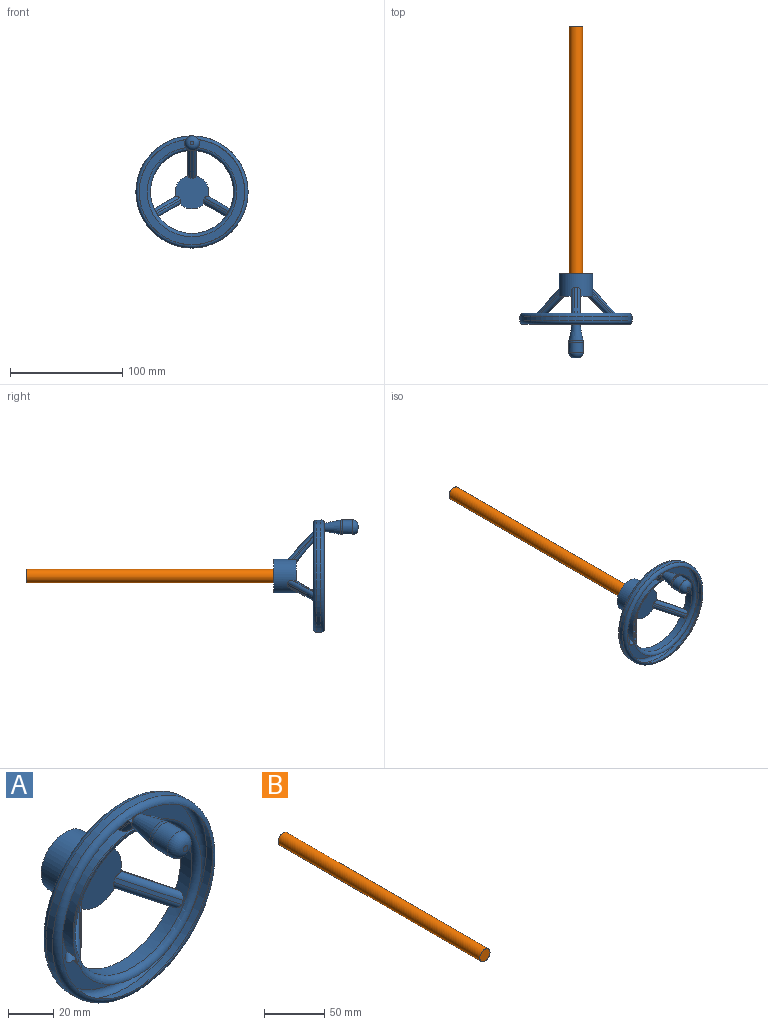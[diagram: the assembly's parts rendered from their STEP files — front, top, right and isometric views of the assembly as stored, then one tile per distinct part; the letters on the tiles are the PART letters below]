
ASSEMBLY  parts=2 mates=1
PART A: 47 faces, bbox 108.3x75x108.3 mm
  f0: cylinder r=15mm len=30mm, axis (0,1,0), area 1712.4mm2, adj f1,f4,f5,f6,f7,f14,f15,f16
  f1: plane 30x29.57mm, normal (0,-1,0), area 663.3mm2, adj f0,f12,f17,f22,f28,f30,f32,f34
  f2: plane 12x12mm, normal (0,1,0), area 113.1mm2, adj f3
  f3: cylinder r=6mm len=15mm, axis (0,1,0), area 565.5mm2, adj f2,f4
  f4: plane 30x30mm, normal (0,1,0), area 593.8mm2, adj f0,f3
  f5: plane 3.25x1.05mm, normal (0,0.32,-0.95), area 0.4mm2, adj f0,f13,f38
  f6: plane 2.99x1.32mm, normal (0.82,0.32,0.47), area 0.4mm2, adj f0,f18,f31
  f7: plane 2.63x1.93mm, normal (-0.82,0.32,0.47), area 0.4mm2, adj f0,f23,f27
  f8: plane 94x94mm, normal (0,-1,0), area 1874.7mm2, adj f39,f41,f42
  f9: cylinder r=37mm len=74mm, axis (0,1,0), area 1500.2mm2, adj f10,f12,f15,f16,f17,f20,f21,f22
  f10: plane 94x94mm, normal (0,1,0), area 2588.2mm2, adj f9,f13,f18,f23,f27,f29,f31,f33
  f11: cylinder r=50mm len=100mm, axis (0,1,0), area 1256.6mm2, adj f40,f41
  f12: plane 24.67x21.04mm, normal (0,-0.76,-0.65), area 64.8mm2, adj f1,f9,f35,f37
  f13: plane 24.73x22.81mm, normal (0,0.74,0.68), area 67.3mm2, adj f5,f10,f14,f36,f38
  f14: plane 3.25x1.05mm, normal (0,0.32,-0.95), area 0.4mm2, adj f0,f13,f36
  f15: plane 22.33x21.12mm, normal (1,0,0), area 29.2mm2, adj f0,f9,f37,f38
  f16: plane 22.33x21.12mm, normal (-1,0,0), area 29.2mm2, adj f0,f9,f35,f36
  f17: plane 22.36x21.04mm, normal (0.56,-0.76,0.32), area 64.8mm2, adj f1,f9,f32,f34
  f18: plane 22.81x22.42mm, normal (-0.59,0.74,-0.34), area 67.3mm2, adj f6,f10,f19,f31,f33
  f19: plane 2.63x1.93mm, normal (0.82,0.32,0.47), area 0.4mm2, adj f0,f18,f33
  f20: plane 21.12x19.34mm, normal (-0.5,0,0.87), area 29.2mm2, adj f0,f9,f31,f34
  f21: plane 21.12x19.34mm, normal (0.5,0,-0.87), area 29.2mm2, adj f0,f9,f32,f33
  f22: plane 22.36x21.04mm, normal (-0.56,-0.76,0.32), area 64.8mm2, adj f1,f9,f28,f30
  f23: plane 22.81x22.42mm, normal (0.59,0.74,-0.34), area 67.3mm2, adj f7,f10,f24,f27,f29
  f24: plane 2.99x1.32mm, normal (-0.82,0.32,0.47), area 0.4mm2, adj f0,f23,f29
  f25: plane 21.12x19.34mm, normal (-0.5,0,-0.87), area 29.2mm2, adj f0,f9,f27,f30
  f26: plane 21.12x19.34mm, normal (0.5,0,0.87), area 29.2mm2, adj f0,f9,f28,f29
  f27: cylinder r=3mm len=25.02mm, axis (-0.64,0.68,0.37), area 151.1mm2, adj f0,f7,f9,f10,f23,f25
  f28: cylinder r=3mm len=24.52mm, axis (-0.66,0.65,0.38), area 144.1mm2, adj f0,f1,f9,f22,f26
  f29: cylinder r=3mm len=25.02mm, axis (0.64,-0.68,-0.37), area 151.1mm2, adj f0,f9,f10,f23,f24,f26
  f30: cylinder r=3mm len=23.29mm, axis (0.66,-0.65,-0.38), area 144.1mm2, adj f0,f1,f9,f22,f25
  f31: cylinder r=3mm len=25.02mm, axis (0.64,0.68,0.37), area 151.1mm2, adj f0,f6,f9,f10,f18,f20
  f32: cylinder r=3mm len=23.29mm, axis (0.66,0.65,0.38), area 144.1mm2, adj f0,f1,f9,f17,f21
  f33: cylinder r=3mm len=25.02mm, axis (-0.64,-0.68,-0.37), area 151.1mm2, adj f0,f9,f10,f18,f19,f21
  f34: cylinder r=3mm len=24.52mm, axis (-0.66,-0.65,-0.38), area 144.1mm2, adj f0,f1,f9,f17,f20
  f35: cylinder r=3mm len=26.58mm, axis (0,0.65,-0.76), area 144.1mm2, adj f0,f1,f9,f12,f16
  f36: cylinder r=3mm len=26.77mm, axis (0,-0.68,0.74), area 151.1mm2, adj f0,f9,f10,f13,f14,f16
  f37: cylinder r=3mm len=26.58mm, axis (0,-0.65,0.76), area 144.1mm2, adj f0,f1,f9,f12,f15
  f38: cylinder r=3mm len=26.77mm, axis (0,0.68,-0.74), area 151.1mm2, adj f0,f5,f9,f10,f13,f15
  f39: torus R=40mm, axis (0,-1,0), area 1127.8mm2, adj f8,f9
  f40: torus R=47mm, axis (0,-1,0), area 1448.2mm2, adj f10,f11
  f41: torus R=47mm, axis (0,-1,0), area 1448.2mm2, adj f8,f11
  f42: cone r=6.5mm half-angle=11.3deg, axis (0,-1,0), area 440.7mm2, adj f8,f46
  f43: cylinder r=6.5mm len=13mm, axis (0,1,0), area 368mm2, adj f45,f46
  f44: plane 3x3mm, normal (0,-1,0), area 7.1mm2, adj f45
  f45: torus R=1.5mm, axis (0,1,0), area 231.1mm2, adj f43,f44
  f46: revolved ~13x13mm, area 159.6mm2, adj f42,f43
PART B: 3 faces, bbox 12x236x12 mm
  f0: cylinder r=6mm len=236mm, axis (0,1,0), area 8897mm2, adj f1,f2
  f1: plane 12x12mm, normal (0,-1,0), area 113.1mm2, adj f0
  f2: plane 12x12mm, normal (0,1,0), area 113.1mm2, adj f0
PLACE A t=(0,-1,0)mm
PLACE B at identity fixed
MATE fastened A.f0 <-> B.f0  axis (0,1,0) through (0,-16,0)mm
